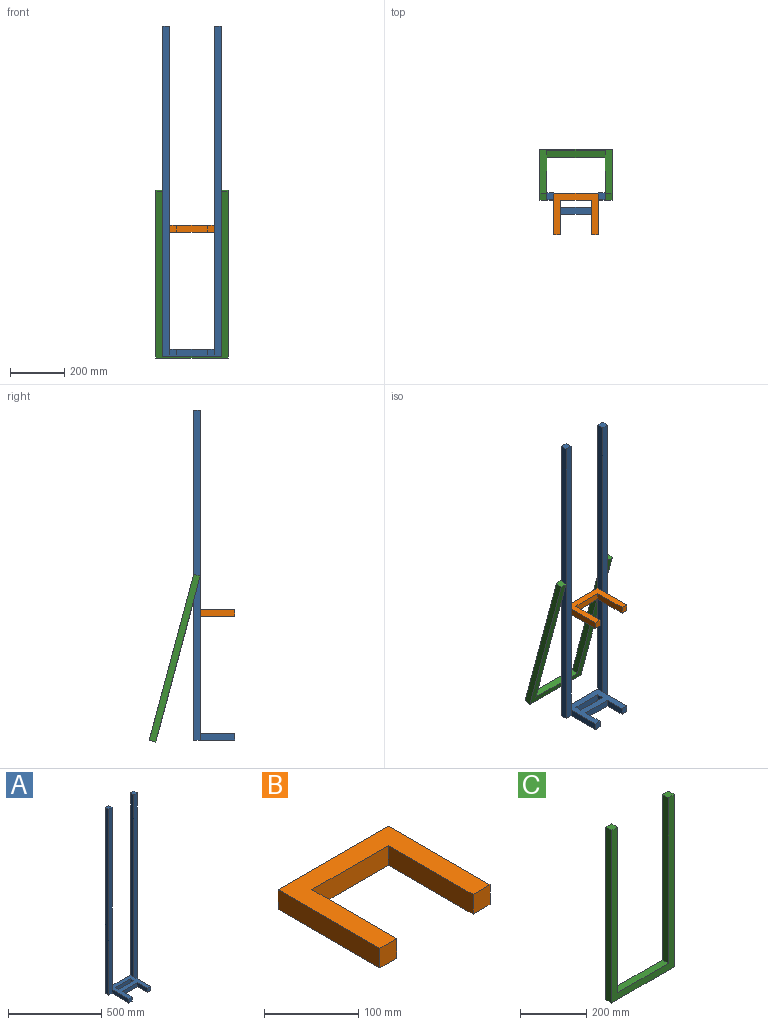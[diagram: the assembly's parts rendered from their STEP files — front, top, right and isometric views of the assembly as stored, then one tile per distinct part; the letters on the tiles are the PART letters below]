
ASSEMBLY  parts=3 mates=2
PART A: 22 faces, bbox 215.9x152.4x1219.2 mm
  f0: plane 25.4x25.4mm, normal (1,0,0), area 645.2mm2, adj f3,f5,f9,f21
  f1: plane 25.4x25.4mm, normal (-1,0,0), area 645.2mm2, adj f3,f5,f9,f21
  f2: plane 1219.2x25.4mm, normal (0,-1,0), area 30967.7mm2, adj f5,f6,f7,f8,f18
  f3: plane 114.3x25.4mm, normal (0,-1,0), area 2903.2mm2, adj f0,f1,f5,f9
  f4: plane 1219.2x25.4mm, normal (-1,0,0), area 30967.7mm2, adj f5,f11,f12,f13
  f5: plane 215.9x152.4mm, normal (0,0,-1), area 14838.7mm2, adj f0,f1,f2,f3,f4,f6,f12,f13
  f6: plane 1219.2x25.4mm, normal (1,0,0), area 30967.7mm2, adj f2,f5,f7,f13
  f7: plane 25.4x25.4mm, normal (0,0,1), area 645.2mm2, adj f2,f6,f8,f13
  f8: plane 1193.8x25.4mm, normal (-1,0,0), area 30322.5mm2, adj f2,f7,f9,f13
  f9: plane 165.1x152.4mm, normal (0,0,1), area 13548.4mm2, adj f0,f1,f3,f8,f10,f13,f14,f15
  f10: plane 1193.8x25.4mm, normal (1,0,0), area 30322.5mm2, adj f9,f11,f12,f13
  f11: plane 25.4x25.4mm, normal (0,0,1), area 645.2mm2, adj f4,f10,f12,f13
  f12: plane 1219.2x25.4mm, normal (0,-1,0), area 30967.7mm2, adj f4,f5,f10,f11,f15
  f13: plane 1219.2x215.9mm, normal (0,1,0), area 66128.9mm2, adj f4,f5,f6,f7,f8,f9,f10,f11
  f14: plane 76.2x25.4mm, normal (1,0,0), area 1935.5mm2, adj f5,f9,f16,f20
  f15: plane 127x25.4mm, normal (-1,0,0), area 3225.8mm2, adj f5,f9,f12,f16
  f16: plane 25.4x25.4mm, normal (0,-1,0), area 645.2mm2, adj f5,f9,f14,f15
  f17: plane 76.2x25.4mm, normal (-1,0,0), area 1935.5mm2, adj f5,f9,f19,f20
  f18: plane 127x25.4mm, normal (1,0,0), area 3225.8mm2, adj f2,f5,f9,f19
  f19: plane 25.4x25.4mm, normal (0,-1,0), area 645.2mm2, adj f5,f9,f17,f18
  f20: plane 114.3x25.4mm, normal (0,-1,0), area 2903.2mm2, adj f5,f9,f14,f17
  f21: plane 114.3x25.4mm, normal (0,1,0), area 2903.2mm2, adj f0,f1,f5,f9
PART B: 10 faces, bbox 165.1x152.4x25.4 mm
  f0: plane 114.3x25.4mm, normal (0,-1,0), area 2903.2mm2, adj f2,f4,f6,f8
  f1: plane 152.4x25.4mm, normal (1,0,0), area 3871mm2, adj f2,f4,f5,f9
  f2: plane 165.1x152.4mm, normal (0,0,1), area 10645.1mm2, adj f0,f1,f3,f5,f6,f7,f8,f9
  f3: plane 152.4x25.4mm, normal (-1,0,0), area 3871mm2, adj f2,f4,f5,f7
  f4: plane 165.1x152.4mm, normal (0,0,-1), area 10645.1mm2, adj f0,f1,f3,f5,f6,f7,f8,f9
  f5: plane 165.1x25.4mm, normal (0,1,0), area 4193.5mm2, adj f1,f2,f3,f4
  f6: plane 127x25.4mm, normal (1,0,0), area 3225.8mm2, adj f0,f2,f4,f7
  f7: plane 25.4x25.4mm, normal (0,-1,0), area 645.2mm2, adj f2,f3,f4,f6
  f8: plane 127x25.4mm, normal (-1,0,0), area 3225.8mm2, adj f0,f2,f4,f9
  f9: plane 25.4x25.4mm, normal (0,-1,0), area 645.2mm2, adj f1,f2,f4,f8
PART C: 10 faces, bbox 266.7x25.4x635 mm
  f0: plane 609.6x25.4mm, normal (-1,0,0), area 15483.8mm2, adj f1,f7,f8,f9
  f1: plane 215.9x25.4mm, normal (0,0,1), area 5483.9mm2, adj f0,f2,f8,f9
  f2: plane 609.6x25.4mm, normal (1,0,0), area 15483.8mm2, adj f1,f3,f8,f9
  f3: plane 25.4x25.4mm, normal (0,0,1), area 645.2mm2, adj f2,f4,f8,f9
  f4: plane 635x25.4mm, normal (-1,0,0), area 16129mm2, adj f3,f5,f8,f9
  f5: plane 266.7x25.4mm, normal (0,0,-1), area 6774.2mm2, adj f4,f6,f8,f9
  f6: plane 635x25.4mm, normal (1,0,0), area 16129mm2, adj f5,f7,f8,f9
  f7: plane 25.4x25.4mm, normal (0,0,1), area 645.2mm2, adj f0,f6,f8,f9
  f8: plane 635x266.7mm, normal (0,-1,0), area 37741.9mm2, adj f0,f1,f2,f3,f4,f5,f6,f7
  f9: plane 635x266.7mm, normal (0,1,0), area 37741.9mm2, adj f0,f1,f2,f3,f4,f5,f6,f7
PLACE A t=(-98.02,23.08,160.24)mm
PLACE B t=(-98.02,23.08,20.54)mm
PLACE C rot(axis=(1,0,0),15deg) t=(-98.02,104.83,-143.15)mm
MATE revolute C.f2 <-> A.f4  axis (1,0,0) through (-205.97,10.38,160.24)mm
MATE fastened B.f3 <-> A.f10  axis (-1,0,0) through (-180.57,-53.12,20.54)mm
